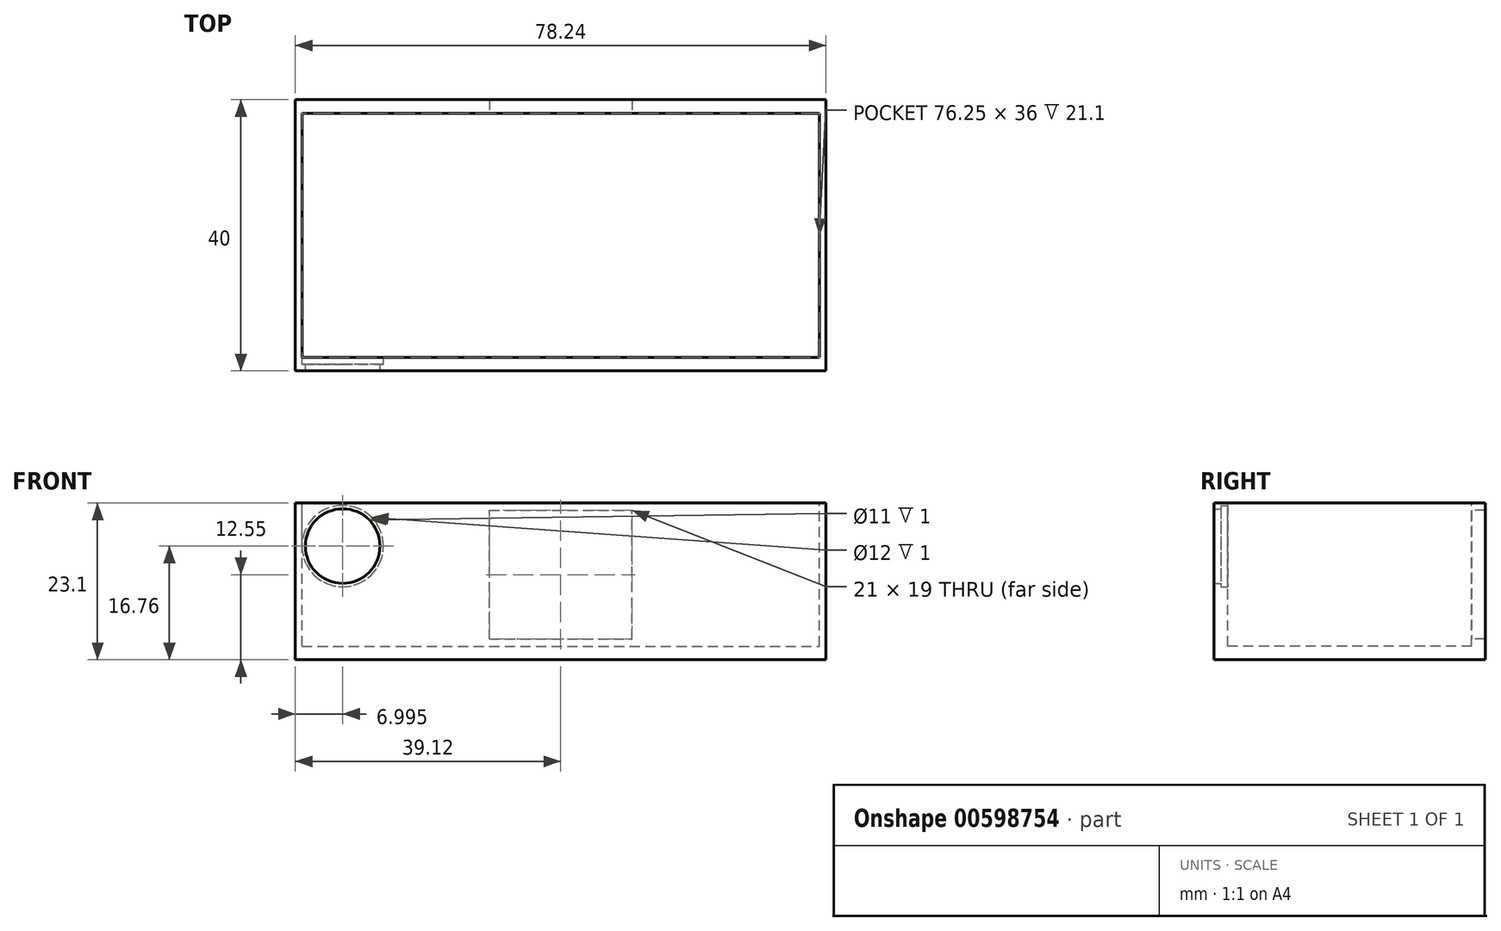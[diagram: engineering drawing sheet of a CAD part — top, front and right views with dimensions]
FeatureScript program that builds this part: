
annotation { "Feature Type Name" : "Feature", "Feature Type Description" : "" }
export const myFeature = defineFeature(function(context is Context, id is Id, definition is map)
    precondition{}
    {
        {
            var Q0;
            Q0=qCreatedBy(makeId("Top.planeOp"),FACE);
            var sketch = newSketch(context, id + "F0", { "sketchPlane" : qUnion([Q0])});
            skLineSegment(sketch, "E0.bottom", {"start": v(-39.12, 20) * mm, "end": v(39.13, 20) * mm});
            skLineSegment(sketch, "E0.top", {"start": v(-39.12, -20) * mm, "end": v(39.12, -20) * mm});
            skLineSegment(sketch, "E0.left", {"start": v(-39.12, 20) * mm, "end": v(-39.13, -20) * mm});
            skLineSegment(sketch, "E0.right", {"start": v(39.13, 20) * mm, "end": v(39.12, -20) * mm});
            skPoint(sketch, "E0.middle", {"position": v(0, 0) * mm});
            skSolve(sketch);
        }
        {
            var Q0;
            Q0=makeQuery(id+"F0.imprint","IMPRINT",FACE,{"disambiguationData":[TD([[makeQuery(id+"F0.imprint","IMPRINT",EDGE,{"derivedFrom":sQuery(id+"F0.wireOp",EDGE,"E0.bottom")}),-1.0]])]});
            extrude(context, id + "F1", {"entities" : qUnion([Q0]), "depth" : 23.1 * mm, "offsetDistance" : 25.4 * mm});
        }
        {
            var Q0;
            Q0=makeQuery(id+"F1.opExtrude","CAP_FACE",FACE,{"disambiguationData":[OSD([sQuery(id+"F0.wireOp",EDGE,"E0.bottom"),sQuery(id+"F0.wireOp",EDGE,"E0.top"),sQuery(id+"F0.wireOp",EDGE,"E0.left"),sQuery(id+"F0.wireOp",EDGE,"E0.right")])],"isStart":false});
            var sketch = newSketch(context, id + "F2", { "sketchPlane" : qUnion([Q0])});
            skLineSegment(sketch, "E1.bottom", {"start": v(-38.12, 18) * mm, "end": v(38.12, 18) * mm});
            skLineSegment(sketch, "E1.top", {"start": v(-38.13, -18) * mm, "end": v(38.12, -18) * mm});
            skLineSegment(sketch, "E1.left", {"start": v(-38.12, 18) * mm, "end": v(-38.12, -18) * mm});
            skLineSegment(sketch, "E1.right", {"start": v(38.12, 18) * mm, "end": v(38.12, -18) * mm});
            skPoint(sketch, "E1.middle", {"position": v(0, 0) * mm});
            skSolve(sketch);
        }
        {
            var Q0;
            Q0=makeQuery(id+"F2.imprint","IMPRINT",FACE,{"disambiguationData":[TD([[makeQuery(id+"F2.imprint","IMPRINT",EDGE,{"derivedFrom":sQuery(id+"F2.wireOp",EDGE,"E1.bottom")}),-1.0]])]});
            extrude(context, id + "F3", {"entities" : qUnion([Q0]), "operationType" : NewBodyOperationType.REMOVE, "oppositeDirection" : true, "depth" : 21.1 * mm, "offsetDistance" : 25.4 * mm});
        }
        {
            var Q0;
            Q0=makeQuery(id+"F3.boolean.opBoolean","COPY",FACE,{"derivedFrom":makeQuery(id+"F3.opExtrude","SWEPT_FACE",FACE,{"disambiguationData":[OSD([sQuery(id+"F2.wireOp",EDGE,"E1.top")])]})});
            var sketch = newSketch(context, id + "F4", { "sketchPlane" : qUnion([Q0])});
            skLineSegment(sketch, "E2", {"start": v(38.12, 2) * mm, "end": v(26.13, 2) * mm});
            skLineSegment(sketch, "E3", {"start": v(32.12, 2) * mm, "end": v(32.12, 16.76) * mm});
            skCircle(sketch, "E4", {"center": v(32.12, 16.76) * mm, "radius": 6 * mm});
            skSolve(sketch);
        }
        {
            var Q0;
            Q0=sQuery(id+"F4.wireOp",VERTEX,"E4.center");
            var Q1;
            Q1=makeQuery(id+"F1.opExtrude","SWEPT_BODY",BODY,{"disambiguationData":[OSD([sQuery(id+"F0.wireOp",EDGE,"E0.bottom"),sQuery(id+"F0.wireOp",EDGE,"E0.top"),sQuery(id+"F0.wireOp",EDGE,"E0.left"),sQuery(id+"F0.wireOp",EDGE,"E0.right")])]});
            hole(context, id + "F5", {"style" : HoleStyle.C_BORE, "endStyle" : HoleEndStyle.BLIND, "holeDiameter" : 11 * mm, "cBoreDiameter" : 12 * mm, "cBoreDepth" : 1 * mm, "majorDiameter" : 6.35 * mm, "holeDepth" : 10 * mm, "isTappedThrough" : true, "tappedDepth" : 12.7 * mm, "tapClearance" : 3, "locations" : qUnion([Q0]), "scope" : qUnion([Q1])});
        }
        {
            var Q0;
            Q0=makeQuery(id+"F3.boolean.opBoolean","COPY",FACE,{"derivedFrom":makeQuery(id+"F3.opExtrude","CAP_FACE",FACE,{"disambiguationData":[OSD([sQuery(id+"F2.wireOp",EDGE,"E1.bottom"),sQuery(id+"F2.wireOp",EDGE,"E1.top"),sQuery(id+"F2.wireOp",EDGE,"E1.left"),sQuery(id+"F2.wireOp",EDGE,"E1.right")])],"isStart":false})});
            var sketch = newSketch(context, id + "F6", { "sketchPlane" : qUnion([Q0])});
            skLineSegment(sketch, "E5", {"start": v(-38.12, -18) * mm, "end": v(-38.12, 17) * mm});
            skLineSegment(sketch, "E6", {"start": v(-38.12, -18) * mm, "end": v(-38.12, 12) * mm});
            skLineSegment(sketch, "E7", {"start": v(-38.12, -18) * mm, "end": v(-26.12, -18) * mm});
            skLineSegment(sketch, "E8", {"start": v(38.12, -18) * mm, "end": v(37.13, -18) * mm});
            skLineSegment(sketch, "E9", {"start": v(37.13, -18) * mm, "end": v(-25.12, -18) * mm});
            skSolve(sketch);
        }
        {
            var Q0;
            Q0=makeQuery(id+"F3.boolean.opBoolean","COPY",FACE,{"derivedFrom":makeQuery(id+"F3.opExtrude","SWEPT_FACE",FACE,{"disambiguationData":[OSD([sQuery(id+"F2.wireOp",EDGE,"E1.bottom")])]})});
            var sketch = newSketch(context, id + "F7", { "sketchPlane" : qUnion([Q0])});
            skLineSegment(sketch, "E10.bottom", {"start": v(10.5, 22.05) * mm, "end": v(-10.5, 22.05) * mm});
            skLineSegment(sketch, "E10.top", {"start": v(10.5, 3.05) * mm, "end": v(-10.5, 3.05) * mm});
            skLineSegment(sketch, "E10.left", {"start": v(10.5, 22.05) * mm, "end": v(10.5, 3.05) * mm});
            skLineSegment(sketch, "E10.right", {"start": v(-10.5, 22.05) * mm, "end": v(-10.5, 3.05) * mm});
            skPoint(sketch, "E10.middle", {"position": v(0, 12.55) * mm});
            skPoint(sketch, "E10.middle.positionSnap0", {"position": v(-38.12, 12.55) * mm});
            skPoint(sketch, "E10.middle.positionSnap1", {"position": v(0, 2) * mm});
            skPoint(sketch, "E10.centerSnap0", {"position": v(-38.12, 12.55) * mm});
            skPoint(sketch, "E10.centerSnap1", {"position": v(0, 2) * mm});
            skSolve(sketch);
        }
        {
            var Q0;
            Q0=makeQuery(id+"F7.imprint","IMPRINT",FACE,{"disambiguationData":[TD([[makeQuery(id+"F7.imprint","IMPRINT",EDGE,{"derivedFrom":sQuery(id+"F7.wireOp",EDGE,"E10.bottom")}),1.0]])]});
            extrude(context, id + "F8", {"entities" : qUnion([Q0]), "operationType" : NewBodyOperationType.REMOVE, "oppositeDirection" : true, "depth" : 25.4 * mm, "offsetDistance" : 25.4 * mm, "hasSecondDirection" : true, "secondDirectionOppositeDirection" : false, "secondDirectionDepth" : 25.4 * mm});
        }
    });
